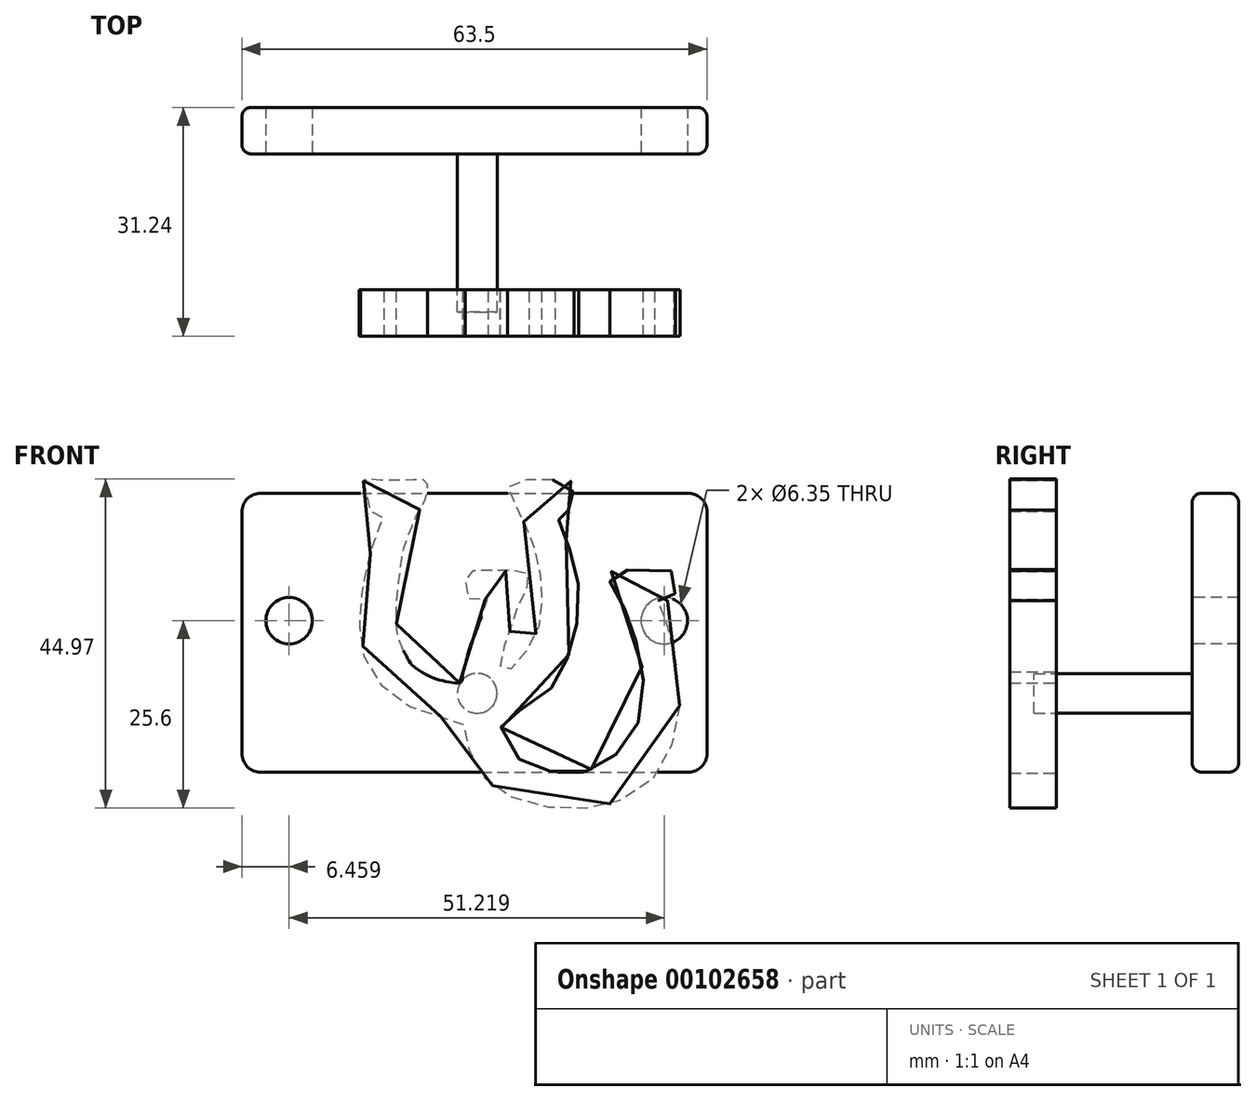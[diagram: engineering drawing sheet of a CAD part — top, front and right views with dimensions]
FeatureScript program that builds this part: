
annotation { "Feature Type Name" : "Feature", "Feature Type Description" : "" }
export const myFeature = defineFeature(function(context is Context, id is Id, definition is map)
    precondition{}
    {
        {
            var Q0;
            Q0=qCreatedBy(makeId("Front.planeOp"),FACE);
            var sketch = newSketch(context, id + "F0", { "sketchPlane" : qUnion([Q0])});
            skLineSegment(sketch, "E0.bottom", {"start": v(-39.5, 30.47) * mm, "end": v(24, 30.47) * mm});
            skLineSegment(sketch, "E0.top", {"start": v(-39.5, -7.63) * mm, "end": v(24, -7.63) * mm});
            skLineSegment(sketch, "E0.left", {"start": v(-39.5, 30.47) * mm, "end": v(-39.5, -7.63) * mm});
            skLineSegment(sketch, "E0.right", {"start": v(24, 30.47) * mm, "end": v(24, -7.63) * mm});
            skSolve(sketch);
        }
        {
            var Q0;
            Q0=makeQuery(id+"F0.imprint","IMPRINT",FACE,{"disambiguationData":[TD([[makeQuery(id+"F0.imprint","IMPRINT",EDGE,{"derivedFrom":sQuery(id+"F0.wireOp",EDGE,"E0.bottom")}),-1.0]])]});
            extrude(context, id + "F1", {"entities" : qUnion([Q0]), "depth" : 6.35 * mm});
        }
        {
            var Q0;
            Q0=makeQuery(id+"F1.opExtrude","SWEPT_EDGE",EDGE,{"disambiguationData":[OSD([sQuery(id+"F0.wireOp",EDGE,"E0.bottom"),sQuery(id+"F0.wireOp",EDGE,"E0.left")])]});
            var Q1;
            Q1=makeQuery(id+"F1.opExtrude","SWEPT_EDGE",EDGE,{"disambiguationData":[OSD([sQuery(id+"F0.wireOp",EDGE,"E0.top"),sQuery(id+"F0.wireOp",EDGE,"E0.left")])]});
            var Q2;
            Q2=makeQuery(id+"F1.opExtrude","SWEPT_EDGE",EDGE,{"disambiguationData":[OSD([sQuery(id+"F0.wireOp",EDGE,"E0.top"),sQuery(id+"F0.wireOp",EDGE,"E0.right")])]});
            var Q3;
            Q3=makeQuery(id+"F1.opExtrude","SWEPT_EDGE",EDGE,{"disambiguationData":[OSD([sQuery(id+"F0.wireOp",EDGE,"E0.bottom"),sQuery(id+"F0.wireOp",EDGE,"E0.right")])]});
            fillet(context, id + "F2", {"entities" : qUnion([Q0, Q1, Q2, Q3]), "radius" : 2.54 * mm, "tangentPropagation" : true, "allowEdgeOverflow" : false});
        }
        {
            var Q0;
            Q0=makeQuery(id+"F1.opExtrude","CAP_EDGE",EDGE,{"disambiguationData":[OSD([sQuery(id+"F0.wireOp",EDGE,"E0.bottom")])],"isStart":false});
            var Q1;
            Q1=makeQuery(id+"F1.opExtrude","CAP_EDGE",EDGE,{"disambiguationData":[OSD([sQuery(id+"F0.wireOp",EDGE,"E0.bottom")])],"isStart":true});
            fillet(context, id + "F3", {"entities" : qUnion([Q0, Q1]), "radius" : 1.27 * mm, "tangentPropagation" : true, "allowEdgeOverflow" : false});
        }
        {
            var Q0;
            Q0=makeQuery(id+"F1.opExtrude","CAP_FACE",FACE,{"disambiguationData":[OSD([sQuery(id+"F0.wireOp",EDGE,"E0.bottom"),sQuery(id+"F0.wireOp",EDGE,"E0.top"),sQuery(id+"F0.wireOp",EDGE,"E0.left"),sQuery(id+"F0.wireOp",EDGE,"E0.right")])],"isStart":false});
            var sketch = newSketch(context, id + "F4", { "sketchPlane" : qUnion([Q0])});
            skCircle(sketch, "E1", {"center": v(-33.05, 13.06) * mm, "radius": 3.18 * mm});
            skCircle(sketch, "E2", {"center": v(18.17, 13.06) * mm, "radius": 3.18 * mm});
            skSolve(sketch);
        }
        {
            var Q0;
            Q0=makeQuery(id+"F4.imprint","IMPRINT",FACE,{"disambiguationData":[TD([[makeQuery(id+"F4.imprint","IMPRINT",EDGE,{"derivedFrom":sQuery(id+"F4.wireOp",EDGE,"E1")}),1.0]])]});
            var Q1;
            Q1=makeQuery(id+"F4.imprint","IMPRINT",FACE,{"disambiguationData":[TD([[makeQuery(id+"F4.imprint","IMPRINT",EDGE,{"derivedFrom":sQuery(id+"F4.wireOp",EDGE,"E2")}),1.0]])]});
            extrude(context, id + "F5", {"entities" : qUnion([Q0, Q1]), "operationType" : NewBodyOperationType.REMOVE, "oppositeDirection" : true, "depth" : 10.4 * mm});
        }
        {
            var Q0;
            Q0=makeQuery(id+"F1.opExtrude","SWEPT_BODY",BODY,{"disambiguationData":[OSD([sQuery(id+"F0.wireOp",EDGE,"E0.bottom"),sQuery(id+"F0.wireOp",EDGE,"E0.top"),sQuery(id+"F0.wireOp",EDGE,"E0.left"),sQuery(id+"F0.wireOp",EDGE,"E0.right")])]});
            transform(context, id + "F6", {"entities" : qUnion([Q0]), "transformType" : TransformType.TRANSLATION_3D, "dx" : 7.37 * mm, "dy" : 0 * mm, "dz" : -13.2 * mm, "makeCopy" : false});
        }
        {
            var Q0;
            Q0=makeQuery(id+"F1.opExtrude","CAP_FACE",FACE,{"disambiguationData":[OSD([sQuery(id+"F0.wireOp",EDGE,"E0.bottom"),sQuery(id+"F0.wireOp",EDGE,"E0.top"),sQuery(id+"F0.wireOp",EDGE,"E0.left"),sQuery(id+"F0.wireOp",EDGE,"E0.right")])],"isStart":false});
            var sketch = newSketch(context, id + "F7", { "sketchPlane" : qUnion([Q0])});
            skCircle(sketch, "E3", {"center": v(0, -10.07) * mm, "radius": 2.72 * mm});
            skSolve(sketch);
        }
        {
            var Q0;
            Q0=makeQuery(id+"F7.imprint","IMPRINT",FACE,{"disambiguationData":[TD([[makeQuery(id+"F7.imprint","IMPRINT",EDGE,{"derivedFrom":sQuery(id+"F7.wireOp",EDGE,"E3")}),1.0]])]});
            extrude(context, id + "F8", {"entities" : qUnion([Q0]), "operationType" : NewBodyOperationType.ADD, "depth" : 21.59 * mm});
        }
        {
            var Q0;
            Q0=qCreatedBy(makeId("Front.planeOp"),FACE);
            var sketch = newSketch(context, id + "F9", { "sketchPlane" : qUnion([Q0])});
            skFitSpline(sketch, "E4", {"points": [v(-17.1, 19.25) * mm, v(-17.14, 16) * mm, v(-15.7, 15.03) * mm, v(-14.52, 15.14) * mm, v(-14.24, 14.75) * mm, v(-14.63, 13.91) * mm, v(-15.43, 11.74) * mm, v(-16.08, 9.5) * mm, v(-16.25, 8.92) * mm, v(-16.65, 7.33) * mm, v(-17.01, 5.73) * mm, v(-17.3, 3.92) * mm, v(-17.45, 2.44) * mm, v(-17.58, -1.03) * mm, v(-17.16, -2.88) * mm, v(-16.9, -5.28) * mm, v(-15.25, -8.03) * mm, v(-13.58, -9.65) * mm, v(-10.62, -11.69) * mm, v(-8.4, -12.47) * mm, v(-5.92, -13.08) * mm, v(-3.6, -13.3) * mm, v(-3.47, -14.25) * mm, v(-3.26, -16.14) * mm, v(-2.42, -18.05) * mm, v(-1.38, -20.07) * mm, v(0, -21.91) * mm, v(2.09, -23.4) * mm, v(5.3, -24.76) * mm, v(8.9, -25.4) * mm, v(12.53, -25.49) * mm, v(15.27, -25.28) * mm, v(18.5, -24.16) * mm, v(21.99, -22.01) * mm, v(24.04, -18.92) * mm, v(25.45, -15.87) * mm, v(26.04, -12.55) * mm, v(26.04, -7.99) * mm, v(25.21, -3.73) * mm, v(24.23, 0) * mm, v(22.76, 2.93) * mm, v(23.12, 2.86) * mm, v(24.5, 2.86) * mm, v(25.06, 3) * mm, v(25.44, 3.64) * mm, v(25.36, 4.94) * mm, v(25.47, 6.56) * mm, v(24.25, 6.96) * mm, v(19.7, 6.98) * mm, v(16.9, 6.93) * mm, v(16.63, 6.11) * mm, v(16.72, 4.89) * mm, v(17.98, 2.9) * mm, v(18.88, 0.91) * mm, v(19.71, -1.5) * mm, v(20.63, -4.28) * mm, v(21.13, -7.92) * mm, v(20.9, -11.73) * mm, v(19.7, -15.74) * mm, v(17.54, -18.1) * mm, v(15.28, -19.57) * mm, v(13.16, -20.53) * mm, v(10.78, -20.72) * mm, v(7.22, -20.23) * mm, v(5.05, -19.57) * mm, v(3.35, -17.62) * mm, v(1.92, -14.9) * mm, v(1.7, -13.08) * mm, v(3.37, -12.5) * mm, v(5.77, -11.31) * mm, v(8.7, -8.93) * mm, v(9.96, -6.85) * mm, v(10.95, -4.66) * mm, v(11.9, -1.75) * mm, v(12.16, 1.27) * mm, v(12.3, 4.81) * mm, v(11.79, 7.53) * mm, v(10.98, 10.08) * mm, v(10.13, 12.42) * mm, v(9.48, 14.16) * mm, v(9.21, 15.2) * mm, v(10.22, 15.25) * mm, v(11.23, 15.3) * mm, v(11.7, 16) * mm, v(11.64, 16.6) * mm, v(11.5, 18.4) * mm, v(11.13, 19.24) * mm, v(8.58, 19.36) * mm, v(5.45, 19.36) * mm, v(3.11, 19.02) * mm, v(2.71, 17.37) * mm, v(3.9, 15.47) * mm, v(4.88, 13.47) * mm, v(5.93, 11.1) * mm, v(6.65, 8.42) * mm, v(7.18, 5.41) * mm, v(7.27, 1.9) * mm, v(6.86, -0.73) * mm, v(5.3, -3.83) * mm, v(3.59, -6.12) * mm, v(2.33, -6.85) * mm, v(1.7, -6.75) * mm, v(2.03, -4.23) * mm, v(2.28, -3.06) * mm, v(2.76, -1.86) * mm, v(3.32, 0) * mm, v(4, 2) * mm, v(4.95, 3.92) * mm, v(5.53, 4.9) * mm, v(5.5, 6.04) * mm, v(5.15, 7.02) * mm, v(3.58, 6.98) * mm, v(1.71, 6.92) * mm, v(0, 6.99) * mm, v(-2.07, 6.89) * mm, v(-2.71, 6.92) * mm, v(-3.15, 5.92) * mm, v(-2.97, 4.32) * mm, v(-2.73, 3.15) * mm, v(-1.04, 3.02) * mm, v(0, 2.9) * mm, v(-0.67, 1.32) * mm, v(-1.64, -1.23) * mm, v(-2.58, -3.64) * mm, v(-3.13, -5.76) * mm, v(-3.53, -7.4) * mm, v(-3.67, -8.31) * mm, v(-5.03, -8.3) * mm, v(-6.9, -7.94) * mm, v(-8.83, -7.06) * mm, v(-10.5, -5.87) * mm, v(-11.18, -4.77) * mm, v(-12.24, -2.46) * mm, v(-12.55, 0) * mm, v(-12.47, 3.34) * mm, v(-11.99, 7.33) * mm, v(-11.6, 9.76) * mm, v(-10.6, 12.59) * mm, v(-9.58, 14.92) * mm, v(-8.58, 16.75) * mm, v(-8.32, 18) * mm, v(-8.5, 19.16) * mm, v(-10.4, 19.32) * mm, v(-12.9, 19.3) * mm, v(-15.73, 19.39) * mm, v(-17.1, 19.25) * mm]});
            skSolve(sketch);
        }
        {
            var Q0;
            Q0=makeQuery(id+"F1.opExtrude","SWEPT_BODY",BODY,{"disambiguationData":[OSD([sQuery(id+"F0.wireOp",EDGE,"E0.bottom"),sQuery(id+"F0.wireOp",EDGE,"E0.top"),sQuery(id+"F0.wireOp",EDGE,"E0.left"),sQuery(id+"F0.wireOp",EDGE,"E0.right")])]});
            transform(context, id + "F10", {"entities" : qUnion([Q0]), "transformType" : TransformType.TRANSLATION_3D, "dx" : 0 * mm, "dy" : 0 * mm, "dz" : 45.97 * mm, "makeCopy" : false});
        }
        {
            var Q0;
            Q0=makeQuery(id+"F9.imprint","IMPRINT",FACE,{"disambiguationData":[TD([[makeQuery(id+"F9.imprint","IMPRINT",EDGE,{"derivedFrom":sQuery(id+"F9.wireOp",EDGE,"E4")}),1.0]])]});
            extrude(context, id + "F11", {"entities" : qUnion([Q0]), "depth" : 6.35 * mm});
        }
        {
            var Q0;
            Q0=makeQuery(id+"F11.opExtrude","SWEPT_BODY",BODY,{"disambiguationData":[OSD([sQuery(id+"F9.wireOp",EDGE,"E4")])]});
            transform(context, id + "F12", {"entities" : qUnion([Q0]), "transformType" : TransformType.TRANSLATION_3D, "dx" : 1.52 * mm, "dy" : -24.9 * mm, "dz" : 45.72 * mm, "makeCopy" : false});
        }
    });
